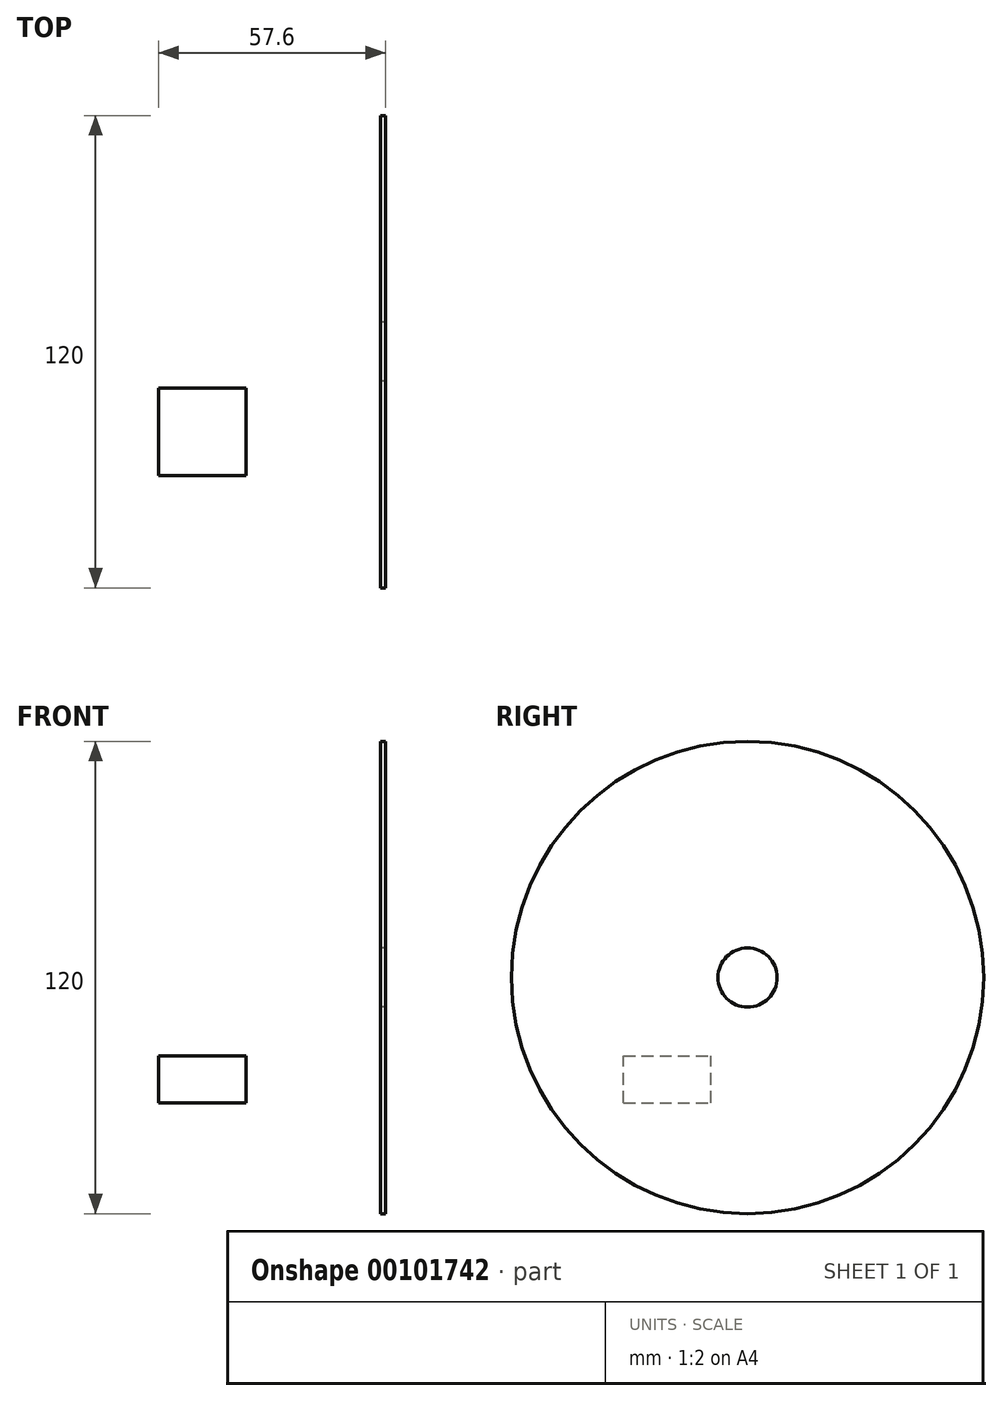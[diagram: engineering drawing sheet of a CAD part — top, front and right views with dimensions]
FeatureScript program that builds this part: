
annotation { "Feature Type Name" : "Feature", "Feature Type Description" : "" }
export const myFeature = defineFeature(function(context is Context, id is Id, definition is map)
    precondition{}
    {
        {
            var Q0;
            Q0=qCreatedBy(makeId("Top.planeOp"),FACE);
            var sketch = newSketch(context, id + "F0", { "sketchPlane" : qUnion([Q0])});
            skLineSegment(sketch, "E0.bottom", {"start": v(-56.4, -41.37) * mm, "end": v(-34.17, -41.37) * mm});
            skLineSegment(sketch, "E0.top", {"start": v(-56.4, -19.15) * mm, "end": v(-34.17, -19.15) * mm});
            skLineSegment(sketch, "E0.left", {"start": v(-56.4, -41.37) * mm, "end": v(-56.4, -19.15) * mm});
            skLineSegment(sketch, "E0.right", {"start": v(-34.17, -41.37) * mm, "end": v(-34.17, -19.15) * mm});
            skSolve(sketch);
        }
        {
            var Q0;
            Q0 = qSketchRegion(id + "F0", true);
            extrude(context, id + "F1", {"entities" : qUnion([Q0]), "oppositeDirection" : true, "depth" : 11.94 * mm});
        }
        {
            var Q0;
            Q0=qCreatedBy(makeId("Right.planeOp"),FACE);
            var sketch = newSketch(context, id + "F2", { "sketchPlane" : qUnion([Q0])});
            skCircle(sketch, "E1", {"center": v(-9.88, 19.9) * mm, "radius": 7.5 * mm});
            skCircle(sketch, "E2", {"center": v(-9.88, 19.9) * mm, "radius": 60 * mm});
            skSolve(sketch);
        }
        {
            var Q0;
            Q0=makeQuery(id+"F2.imprint","IMPRINT",FACE,{"disambiguationData":[TD([[makeQuery(id+"F2.imprint","IMPRINT",EDGE,{"derivedFrom":sQuery(id+"F2.wireOp",EDGE,"E1")}),-1.0]])]});
            extrude(context, id + "F3", {"entities" : qUnion([Q0]), "depth" : 1.2 * mm});
        }
    });
